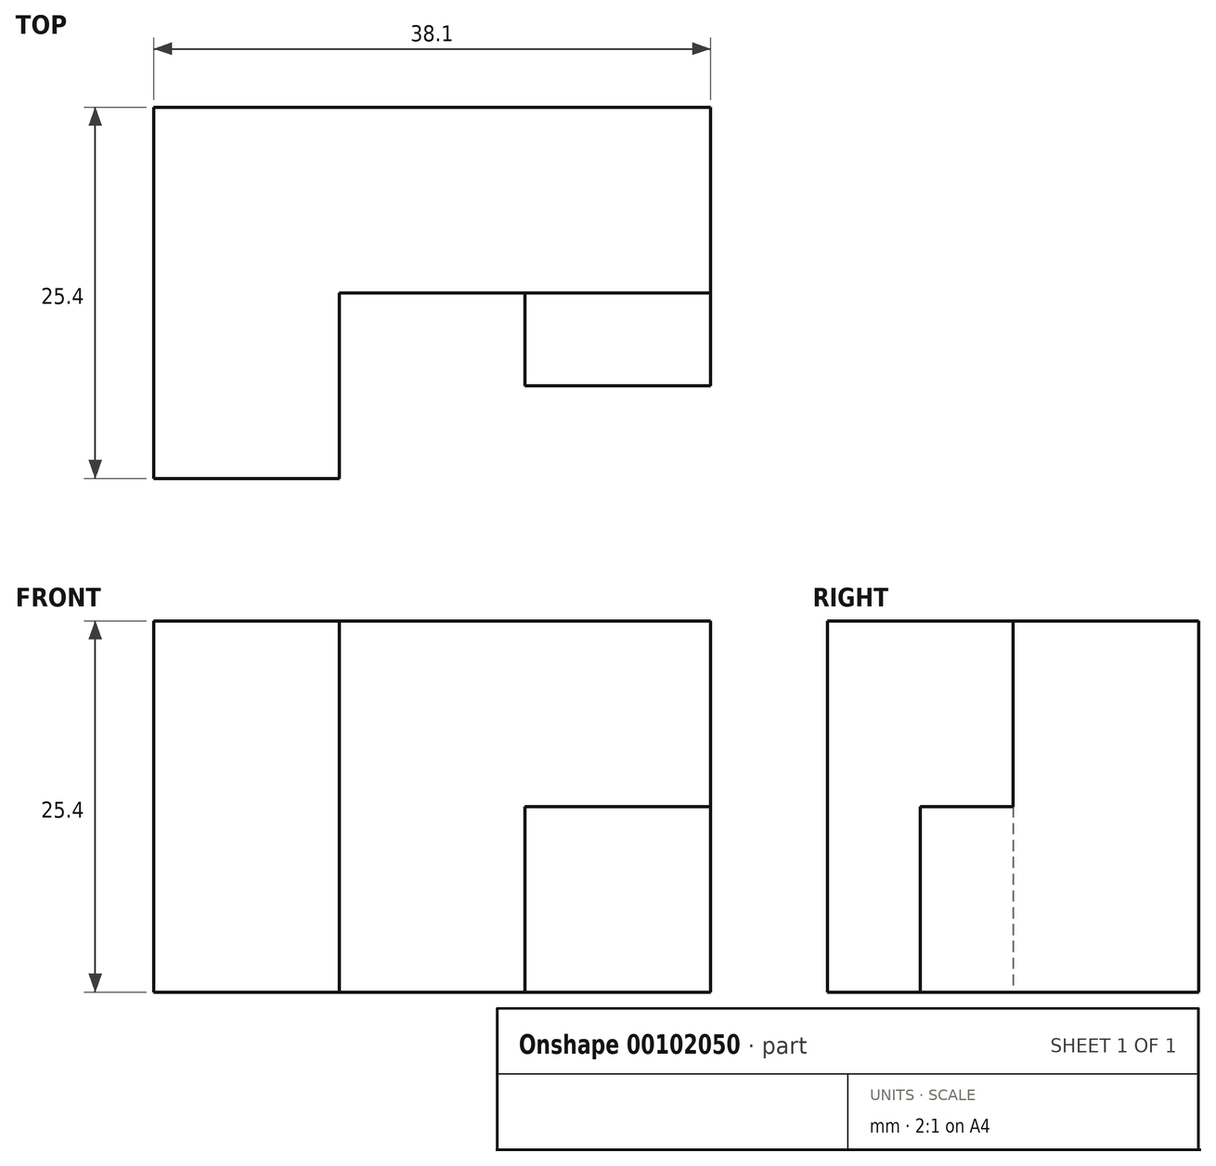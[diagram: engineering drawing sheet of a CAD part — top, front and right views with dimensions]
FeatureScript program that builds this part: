
annotation { "Feature Type Name" : "Feature", "Feature Type Description" : "" }
export const myFeature = defineFeature(function(context is Context, id is Id, definition is map)
    precondition{}
    {
        {
            var Q0;
            Q0=qCreatedBy(makeId("Top.planeOp"),FACE);
            var sketch = newSketch(context, id + "F0", { "sketchPlane" : qUnion([Q0])});
            skLineSegment(sketch, "E0", {"start": v(0, 0) * mm, "end": v(0, 25.4) * mm});
            skLineSegment(sketch, "E1", {"start": v(0, 25.4) * mm, "end": v(38.1, 25.4) * mm});
            skLineSegment(sketch, "E2", {"start": v(38.1, 25.4) * mm, "end": v(38.1, 12.7) * mm});
            skLineSegment(sketch, "E3", {"start": v(0, 0) * mm, "end": v(12.7, 0) * mm});
            skLineSegment(sketch, "E4", {"start": v(38.1, 12.7) * mm, "end": v(12.7, 12.7) * mm});
            skLineSegment(sketch, "E5", {"start": v(12.7, 12.7) * mm, "end": v(12.7, 0) * mm});
            skLineSegment(sketch, "E6", {"start": v(38.1, 12.7) * mm, "end": v(38.1, 6.35) * mm});
            skLineSegment(sketch, "E7", {"start": v(38.1, 6.35) * mm, "end": v(25.4, 6.35) * mm});
            skLineSegment(sketch, "E8", {"start": v(25.4, 6.35) * mm, "end": v(25.4, 12.7) * mm});
            skSolve(sketch);
        }
        {
            var Q0;
            Q0=makeQuery(id+"F0.imprint","IMPRINT",FACE,{"disambiguationData":[TD([[makeQuery(id+"F0.imprint","IMPRINT",EDGE,{"derivedFrom":sQuery(id+"F0.wireOp",EDGE,"E0")}),-1.0]])]});
            extrude(context, id + "F1", {"entities" : qUnion([Q0]), "depth" : 25.4 * mm});
        }
        {
            var Q0;
            {var subQ0=sQuery(id+"F0.wireOp",EDGE,"E6");Q0=makeQuery(id+"F0.imprint","IMPRINT",FACE,{"disambiguationData":[TD([[makeQuery(id+"F0.imprint","IMPRINT",EDGE,{"derivedFrom":subQ0}),-1.0]])]});}
            extrude(context, id + "F2", {"entities" : qUnion([Q0]), "operationType" : NewBodyOperationType.ADD, "depth" : 12.7 * mm});
        }
    });
